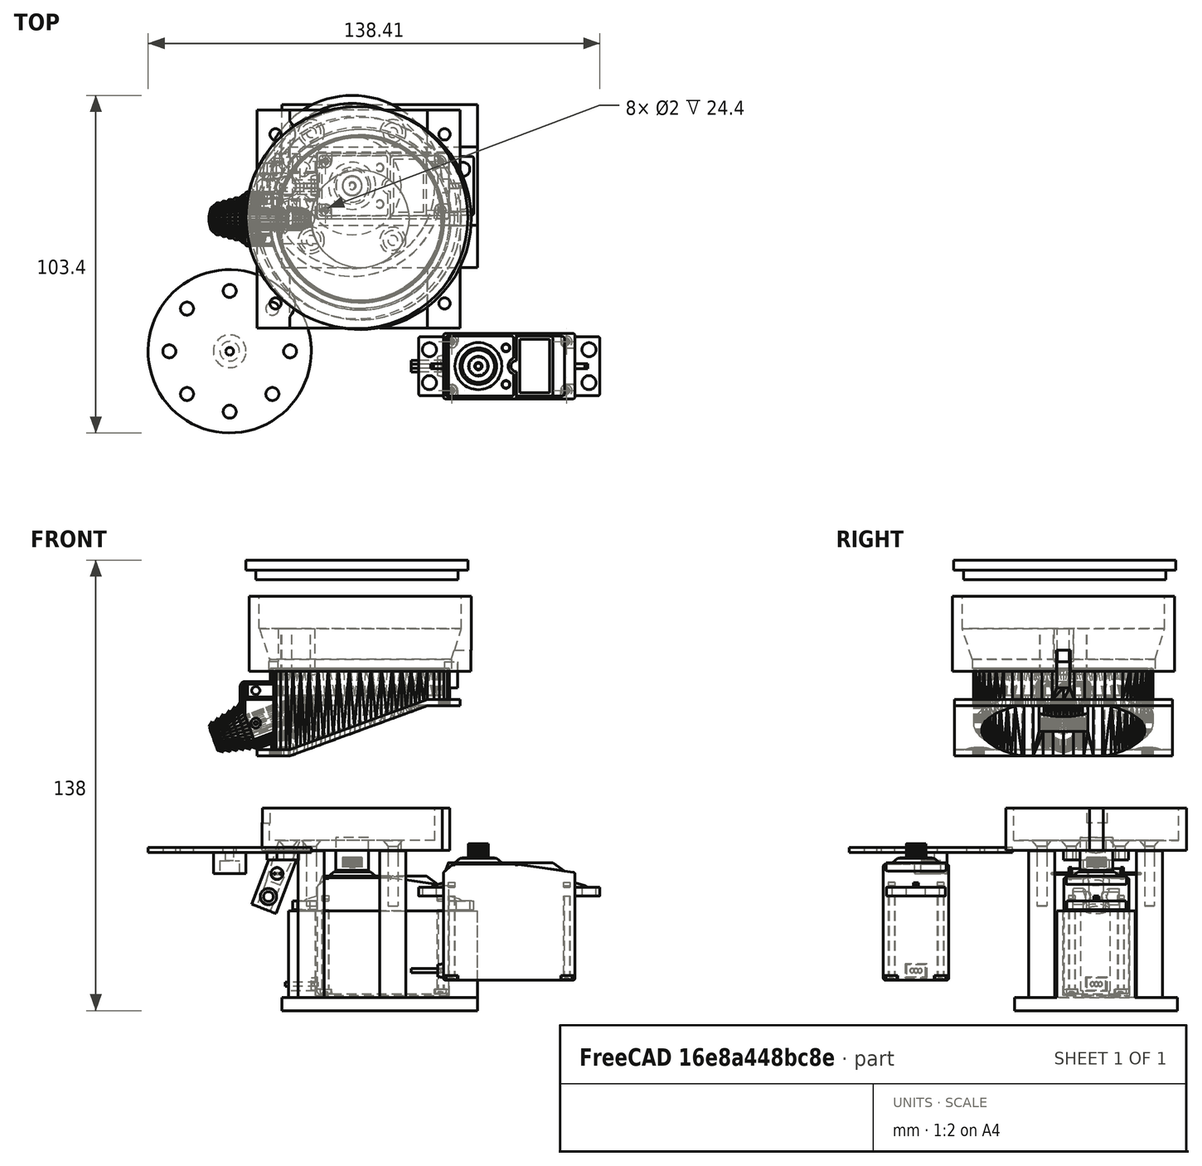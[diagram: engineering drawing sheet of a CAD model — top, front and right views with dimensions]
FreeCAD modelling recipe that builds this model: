
FCSTD DOCUMENT  (FreeCAD 0.21R33694 (Git))
Label: all_parts_chute_with_mount_v4
License: All rights reserved
LicenseURL: http://en.wikipedia.org/wiki/All_rights_reserved
objects: Part::Cylinder×34, Part::Cut×23, Part::MultiFuse×21, Part::Feature×18, Part::Box×11, Part::FeaturePython×5, Part::Cone×2, Sketcher::SketchObject×2, Part::Extrusion×2, Mesh::Feature×1, Part::Fillet×1, Part::Chamfer×1
note: 120 computed .brp shape members not serialized (recipe doc carries the construction recipe); baked Part::Feature solids carry a one-line shape summary decoded from their .brp

FEATURE [Part::Box] Box014  label="Cube014"
  AttacherType = Attacher::AttachEngine3D
  Height = 13
  Length = 4.2
  Placement = pos=(66.2,37.3,63.6) rot=(0,0,1;0rad)
  Width = 4.2
FEATURE [Part::Cylinder] Cylinder022
  Angle = 360
  AttacherType = Attacher::AttachEngine3D
  FirstAngle = 0
  Height = 20
  Placement = pos=(15.5,39.3,51.5) rot=(0,1,0;0.366519rad)
  Radius = 3
  SecondAngle = 0
FEATURE [Part::Box] Box015  label="Cube015"
  AttacherType = Attacher::AttachEngine3D
  Height = 10
  Length = 10
  Placement = pos=(7,36.6,72) rot=(0,0,1;0rad)
  Width = 6.2
FEATURE [Mesh::Feature] Base_V7  label="Base V7"
FEATURE [Part::Feature] Base_V7001_solid  label="hopper (Solid)"
  shape: bbox 76.98 x 66.8 x 28.84 mm, 5900 faces (baked)
FEATURE [Part::Feature] Shape001
  Placement = pos=(47,50.7,-44.8) rot=(0,0,1;3.14159rad)
  shape: bbox 57.75 x 20 x 41.74 mm, 378 faces, 4 solids (baked)
FEATURE [Part::Cylinder] cylinder010  label="servo_central_shaft"
  Angle = 360
  AttacherType = Attacher::AttachEngine3D
  FirstAngle = 0
  Height = 10
  Placement = pos=(37.55,50.7,-7) rot=(0,0,1;0rad)
  Radius = 5
  SecondAngle = 0
FEATURE [Part::Box] Box  label="Cube"
  AttacherType = Attacher::AttachEngine3D
  Height = 27.5
  Length = 58
  Placement = pos=(18,38.6,-47) rot=(0,0,1;0rad)
  Width = 24
FEATURE [Part::Box] Box016  label="Cube016"
  AttacherType = Attacher::AttachEngine3D
  Height = 29.5
  Length = 53
  Placement = pos=(13,46,-44) rot=(0,0,1;0rad)
  Width = 9
FEATURE [Part::Cut] Cut
  Base = -> Box
  Tool = -> Box016
FEATURE [Part::Box] Box017  label="Cube017"
  AttacherType = Attacher::AttachEngine3D
  Height = 29.5
  Length = 10
  Placement = pos=(17,46.6,-46) rot=(0,0,1;0rad)
  Width = 8
FEATURE [Part::Cut] Cut019
  Base = -> Cut
  Tool = -> Box017
FEATURE [Part::Box] Box018  label="Cube018"
  AttacherType = Attacher::AttachEngine3D
  Height = 27.5
  Length = 41
  Placement = pos=(0.5,50.4,-44.2) rot=(0,0,1;0rad)
  Width = 20.4
FEATURE [Part::Fillet] Fillet
  Base = -> Box018
  Edges = 4 edges r=1: [Edge1,Edge3,Edge5,Edge7]
  Placement = pos=(25.85,-9.87885,-1.16822) rot=(0,0,1;0rad)
FEATURE [Part::Cut] Cut020
  Base = -> Cut019
  Tool = -> Fillet
FEATURE [Part::Box] Box020  label="base_plate"
  AttacherType = Attacher::AttachEngine3D
  Height = 4
  Length = 60
  Placement = pos=(16,25.6,-50) rot=(0,0,1;0rad)
  Width = 50
FEATURE [Part::Feature] BOLTS_part  label="Hex socket countersunk head screw M3 20.0"
  Placement = pos=(25,67,2.1) rot=(0,1,0;3.14159rad)
  shape: bbox 6 x 6 x 20 mm, 12 faces (baked)
FEATURE [Part::Feature] BOLTS_part001  label="Hex socket countersunk head screw M3 20.001"
  Placement = pos=(50,67,2.1) rot=(0,1,0;3.14159rad)
  shape: bbox 6 x 6 x 20 mm, 12 faces (baked)
FEATURE [Part::Feature] BOLTS_part002  label="Hex socket countersunk head screw M3 20.002"
  Placement = pos=(50,34,2.1) rot=(0,1,0;3.14159rad)
  shape: bbox 6 x 6 x 20 mm, 12 faces (baked)
FEATURE [Part::Feature] BOLTS_part003  label="Hex socket countersunk head screw M3 20.003"
  Placement = pos=(25,34,2.1) rot=(0,1,0;3.14159rad)
  shape: bbox 6 x 6 x 20 mm, 12 faces (baked)
FEATURE [Part::Cylinder] Cylinder024
  Angle = 360
  AttacherType = Attacher::AttachEngine3D
  FirstAngle = 0
  Height = 48
  Placement = pos=(50,67,-49) rot=(0,0,1;0rad)
  Radius = 4
  SecondAngle = 0
FEATURE [Part::Cylinder] Cylinder025
  Angle = 360
  AttacherType = Attacher::AttachEngine3D
  FirstAngle = 0
  Height = 48
  Placement = pos=(25,34,-49) rot=(0,0,1;0rad)
  Radius = 4
  SecondAngle = 0
FEATURE [Part::Cylinder] Cylinder026
  Angle = 360
  AttacherType = Attacher::AttachEngine3D
  FirstAngle = 0
  Height = 48
  Placement = pos=(25,67,-49) rot=(0,0,1;0rad)
  Radius = 4
  SecondAngle = 0
FEATURE [Part::Cylinder] Cylinder027
  Angle = 360
  AttacherType = Attacher::AttachEngine3D
  FirstAngle = 0
  Height = 48
  Placement = pos=(50,34,-49) rot=(0,0,1;0rad)
  Radius = 4
  SecondAngle = 0
FEATURE [Part::Feature] Shape002  label="led2"
  Placement = pos=(14.5,42.3,-8) rot=(-1,0,0;1.5708rad)
  shape: bbox 3.686 x 11.4 x 3.686 mm, 26 faces, 3 solids (baked)
FEATURE [Part::Feature] Shape003  label="led1"
  Placement = pos=(14.5,59.1,-8) rot=(1,0,0;1.5708rad)
  shape: bbox 3.686 x 11.4 x 3.686 mm, 26 faces, 3 solids (baked)
FEATURE [Part::Feature] BOLTS_part004  label="Hex socket countersunk head screw M3 20.004"
  Placement = pos=(25,34,2.05) rot=(0,1,0;3.14159rad)
  shape: bbox 6 x 6 x 20 mm, 12 faces (baked)
FEATURE [Part::Feature] BOLTS_part005  label="Hex socket countersunk head screw M3 20.005"
  Placement = pos=(50,34,2.05) rot=(0,1,0;3.14159rad)
  shape: bbox 6 x 6 x 20 mm, 12 faces (baked)
FEATURE [Part::Feature] BOLTS_part006  label="Hex socket countersunk head screw M3 20.006"
  Placement = pos=(50,67,2.05) rot=(0,1,0;3.14159rad)
  shape: bbox 6 x 6 x 20 mm, 12 faces (baked)
FEATURE [Part::Feature] BOLTS_part007  label="Hex socket countersunk head screw M3 20.007"
  Placement = pos=(25,67,2.05) rot=(0,1,0;3.14159rad)
  shape: bbox 6 x 6 x 20 mm, 12 faces (baked)
FEATURE [Part::Cylinder] Cylinder032
  Angle = 360
  AttacherType = Attacher::AttachEngine3D
  FirstAngle = 0
  Height = 48
  Placement = pos=(50,67,-43) rot=(0,0,1;0rad)
  Radius = 1.4
  SecondAngle = 0
FEATURE [Part::Cylinder] Cylinder033
  Angle = 360
  AttacherType = Attacher::AttachEngine3D
  FirstAngle = 0
  Height = 48
  Placement = pos=(25,34,-43) rot=(0,0,1;0rad)
  Radius = 1.4
  SecondAngle = 0
FEATURE [Part::Cylinder] Cylinder034
  Angle = 360
  AttacherType = Attacher::AttachEngine3D
  FirstAngle = 0
  Height = 48
  Placement = pos=(25,67,-42) rot=(0,0,1;0rad)
  Radius = 1.4
  SecondAngle = 0
FEATURE [Part::Cylinder] Cylinder035
  Angle = 360
  AttacherType = Attacher::AttachEngine3D
  FirstAngle = 0
  Height = 48
  Placement = pos=(50,34,-43) rot=(0,0,1;0rad)
  Radius = 1.4
  SecondAngle = 0
FEATURE [Part::Cut] Cut030
  Base = -> Cylinder024
  Tool = -> BOLTS_part006
FEATURE [Part::Cut] Cut031
  Base = -> Cylinder025
  Tool = -> BOLTS_part004
FEATURE [Part::Cut] Cut032
  Base = -> Cylinder026
  Tool = -> BOLTS_part007
FEATURE [Part::Cut] Cut033
  Base = -> Cylinder027
  Tool = -> BOLTS_part005
FEATURE [Part::MultiFuse] Fusion011  label="motor_holder"
  Shapes = -> [Cut020,Cut030,Cut031,Cut032,Cut033,Box020]
FEATURE [Part::Cylinder] Cylinder039
  Angle = 360
  AttacherType = Attacher::AttachEngine3D
  FirstAngle = 0
  Height = 21
  Placement = pos=(0,10,4) rot=(1,0,0;1.5708rad)
  Radius = 1.5
  SecondAngle = 0
FEATURE [Part::FeaturePython] Tube003  # WARN: FeaturePython — macro-defined, semantics opaque (R4)
  AttacherType = Attacher::AttachEngine3D
  Height = 5
  InnerRadius = 1.5
  OuterRadius = 2.5
  Placement = pos=(0,2.05,4) rot=(-1,0,0;1.5708rad)
FEATURE [Part::FeaturePython] Tube004  # WARN: FeaturePython — macro-defined, semantics opaque (R4)
  AttacherType = Attacher::AttachEngine3D
  Height = 5
  InnerRadius = 1.5
  OuterRadius = 2.5
  Placement = pos=(0,-2.05,4) rot=(1,0,0;1.5708rad)
FEATURE [Part::Box] Box021  label="Cube019"
  AttacherType = Attacher::AttachEngine3D
  Height = 10
  Length = 20
  Placement = pos=(1.17,-11.94,17.9) rot=(0,0,1;0rad)
  Width = 24
FEATURE [Part::FeaturePython] Tube001  # WARN: FeaturePython — macro-defined, semantics opaque (R4)
  AttacherType = Attacher::AttachEngine3D
  Height = 3
  InnerRadius = 15
  OuterRadius = 27.7
  Placement = pos=(40.45,39.4,63.6) rot=(0,0,1;0rad)
FEATURE [Part::FeaturePython] Tube002  # WARN: FeaturePython — macro-defined, semantics opaque (R4)
  AttacherType = Attacher::AttachEngine3D
  Height = 13
  InnerRadius = 25.3
  OuterRadius = 27.7
  Placement = pos=(40.45,39.4,63.6) rot=(0,0,1;0rad)
FEATURE [Part::MultiFuse] Fusion009
  Shapes = -> [Box014,Tube001,Tube002]
FEATURE [Part::Cut] Cut014  label="cut"
  Base = -> Fusion009
  Tool = -> Cylinder022
FEATURE [Part::Cut] Cut036
  Base = -> Cut014
  Placement = pos=(-2.9,11.3,-64.5) rot=(0,0,1;0rad)
  Tool = -> Box015
FEATURE [Part::MultiFuse] Fusion
  Shapes = -> [BOLTS_part003,Cylinder033]
FEATURE [Part::MultiFuse] Fusion013
  Shapes = -> [BOLTS_part002,Cylinder035]
FEATURE [Part::MultiFuse] Fusion014
  Shapes = -> [BOLTS_part001,Cylinder032]
FEATURE [Part::MultiFuse] Fusion015
  Shapes = -> [BOLTS_part,Cylinder034]
FEATURE [Part::Cut] Cut037
  Base = -> Cut036
  Tool = -> Fusion
FEATURE [Part::Cut] Cut038
  Base = -> Cut037
  Tool = -> Fusion013
FEATURE [Part::Cut] Cut039
  Base = -> Cut038
  Tool = -> Fusion015
FEATURE [Part::Cut] Cut040
  Base = -> Cut039
  Tool = -> Fusion014
FEATURE [Part::Feature] BOLTS_part009  label="Hex socket countersunk head screw M3 20.008"
  Placement = pos=(50,34,2.1) rot=(0,1,0;3.14159rad)
  shape: bbox 6 x 6 x 20 mm, 12 faces (baked)
FEATURE [Part::Cylinder] Cylinder040
  Angle = 360
  AttacherType = Attacher::AttachEngine3D
  FirstAngle = 0
  Height = 48
  Placement = pos=(50,34,-43) rot=(0,0,1;0rad)
  Radius = 1.4
  SecondAngle = 0
FEATURE [Part::MultiFuse] Fusion016
  Placement = pos=(-32,9,0) rot=(0,0,1;0rad)
  Shapes = -> [BOLTS_part009,Cylinder040]
FEATURE [Part::Feature] BOLTS_part010  label="Hex socket countersunk head screw M3 20.009"
  Placement = pos=(50,34,2.1) rot=(0,1,0;3.14159rad)
  shape: bbox 6 x 6 x 20 mm, 12 faces (baked)
FEATURE [Part::Cylinder] Cylinder041
  Angle = 360
  AttacherType = Attacher::AttachEngine3D
  FirstAngle = 0
  Height = 48
  Placement = pos=(50,34,-43) rot=(0,0,1;0rad)
  Radius = 1.4
  SecondAngle = 0
FEATURE [Part::MultiFuse] Fusion017
  Placement = pos=(-32,24,0) rot=(0,0,1;0rad)
  Shapes = -> [BOLTS_part010,Cylinder041]
FEATURE [Part::Box] Box022  label="Cube020"
  AttacherType = Attacher::AttachEngine3D
  Height = 3
  Length = 10
  Placement = pos=(3,-10,15) rot=(0,0,1;0rad)
  Width = 20
FEATURE [Part::Cylinder] Cylinder
  Angle = 360
  AttacherType = Attacher::AttachEngine3D
  FirstAngle = 0
  Height = 18
  Radius = 4
  SecondAngle = 0
FEATURE [Part::Cut] Cut043
  Base = -> Cylinder
  Tool = -> Cylinder039
FEATURE [Part::MultiFuse] Fusion018
  Placement = pos=(2,0,0) rot=(0,1,0;0.366519rad)
  Shapes = -> [Tube003,Tube004,Cut043]
FEATURE [Part::MultiFuse] Fusion019
  Shapes = -> [Fusion018,Box022]
FEATURE [Part::Feature] BOLTS_part011  label="Hex socket countersunk head screw M3 20.010"
  Placement = pos=(50,34,2.1) rot=(0,1,0;3.14159rad)
  shape: bbox 6 x 6 x 20 mm, 12 faces (baked)
FEATURE [Part::Cylinder] Cylinder044
  Angle = 360
  AttacherType = Attacher::AttachEngine3D
  FirstAngle = 0
  Height = 48
  Placement = pos=(50,34,-43) rot=(0,0,1;0rad)
  Radius = 1.4
  SecondAngle = 0
FEATURE [Part::MultiFuse] Fusion021
  Placement = pos=(-32,9,0) rot=(0,0,1;0rad)
  Shapes = -> [BOLTS_part011,Cylinder044]
FEATURE [Part::Feature] BOLTS_part012  label="Hex socket countersunk head screw M3 20.011"
  Placement = pos=(50,34,2.1) rot=(0,1,0;3.14159rad)
  shape: bbox 6 x 6 x 20 mm, 12 faces (baked)
FEATURE [Part::Cylinder] Cylinder045
  Angle = 360
  AttacherType = Attacher::AttachEngine3D
  FirstAngle = 0
  Height = 48
  Placement = pos=(50,34,-43) rot=(0,0,1;0rad)
  Radius = 1.4
  SecondAngle = 0
FEATURE [Part::MultiFuse] Fusion022
  Placement = pos=(-32,24,0) rot=(0,0,1;0rad)
  Shapes = -> [BOLTS_part012,Cylinder045]
FEATURE [Part::Cut] Cut047
  Base = -> Cut040
  Tool = -> Fusion016
FEATURE [Part::Cut] Cut048  label="base"
  Base = -> Cut047
  Tool = -> Fusion017
FEATURE [Part::Feature] Shape004
  Placement = pos=(85.6641,-4.55315,-40.6487) rot=(0,0,1;3.14159rad)
  shape: bbox 57.75 x 20 x 41.74 mm, 378 faces, 4 solids (baked)
FEATURE [Part::Box] Box012  label="Cube012"
  AttacherType = Attacher::AttachEngine3D
  Height = 10
  Length = 10
  Placement = pos=(7,36.17,76) rot=(0,0,1;0rad)
  Width = 6
FEATURE [Part::Box] Box013  label="Cube013"
  AttacherType = Attacher::AttachEngine3D
  Height = 10
  Length = 14
  Placement = pos=(64,38.5,50.5) rot=(0,0,1;0rad)
  Width = 4.3
FEATURE [Part::Cone] Cone
  Angle = 360
  AttacherType = Attacher::AttachEngine3D
  Height = 14
  Placement = pos=(40,40.65,53) rot=(0,0,1;0rad)
  Radius1 = 26.5
  Radius2 = 31
FEATURE [Part::Cylinder] Cylinder019
  Angle = 360
  AttacherType = Attacher::AttachEngine3D
  FirstAngle = 0
  Height = 13
  Placement = pos=(40,40.65,54) rot=(0,0,1;0rad)
  Radius = 34
  SecondAngle = 0
FEATURE [Part::Cylinder] Cylinder020
  Angle = 360
  AttacherType = Attacher::AttachEngine3D
  FirstAngle = 0
  Height = 13
  Placement = pos=(40,39.2,54) rot=(0,0,1;0rad)
  Radius = 25
  SecondAngle = 0
FEATURE [Part::Cylinder] Cylinder021
  Angle = 360
  AttacherType = Attacher::AttachEngine3D
  FirstAngle = 0
  Height = 4
  Placement = pos=(40,40.65,54) rot=(0,0,1;0rad)
  Radius = 28
  SecondAngle = 0
FEATURE [Sketcher::SketchObject] Sketch001
  FullyConstrained = true
  MapMode = 2
  Placement = pos=(0,5,65) rot=(0,0,1;0rad)
  sketch-geometry (8):
    g0: ArcOfCircle CenterX=20.555 CenterY=41.4363 CenterZ=0 NormalX=0 NormalY=0 NormalZ=1 AngleXU=0 Radius=4.5 StartAngle=3.17145 EndAngle=4.38602
    g1: ArcOfCircle CenterX=24.0176 CenterY=34.022 CenterZ=0 NormalX=0 NormalY=0 NormalZ=1 AngleXU=0 Radius=2 StartAngle=5.10518 EndAngle=7.46119
    g2: ArcOfCircle CenterX=20.5312 CenterY=26.882 CenterZ=0 NormalX=0 NormalY=0 NormalZ=1 AngleXU=0 Radius=4.5 StartAngle=1.8916 EndAngle=3.11914
    g3: LineSegment StartX=19.1123 StartY=31.1525 StartZ=0 EndX=24.7831 EndY=32.1743 EndZ=0
    g4: LineSegment StartX=19.1123 StartY=37.1738 StartZ=0 EndX=24.7831 EndY=35.8697 EndZ=0
    g5: LineSegment StartX=16.057 StartY=41.302 StartZ=0 EndX=15.8089 EndY=41.3763 EndZ=0
    g6: LineSegment StartX=15.8133 StartY=26.9187 StartZ=0 EndX=16.0324 EndY=26.9831 EndZ=0
    g7: ArcOfCircle CenterX=39.7432 CenterY=34.1548 CenterZ=0 NormalX=0 NormalY=0 NormalZ=1 AngleXU=0 Radius=25 StartAngle=2.84856 EndAngle=3.43524
  constraints (28):
    c: Coincident(g3,g2)
    c: Coincident(g3,g1)
    c: Coincident(g4,g0)
    c: Coincident(g4,g1)
    c: Coincident(g5,g0)
    c: Coincident(g6,g2)
    c: Coincident(g7,g6)
    c: Coincident(g7,g5)
    c: Radius(g2) = 4.5
    c: Radius(g0) = 4.5
    c: Radius(g1) = 2
    c: Radius(g7) = 25
    c: DistanceX(g5) = 15.8089
    c: DistanceY(g5) = 41.3763
    c: DistanceX(g2) = 16.0324
    c: DistanceY(g2) = 26.9831
    c: DistanceX(g3) = 19.1123
    c: DistanceY(g3) = 31.1525
    c: DistanceX(g2,g0) = 0
    c: DistanceX(g3,g1) = 0
    c: DistanceX(g1) = 24.7831
    c: DistanceY(g1) = 32.1743
    c: DistanceX(g5) = 16.057
    c: DistanceY(g5) = 41.302
    c: DistanceX(g7) = 15.8133
    c: DistanceY(g7) = 26.9187
    c: DistanceY(g1) = 35.8697
    c: DistanceY(g0) = 37.1738
FEATURE [Part::Extrusion] Extrude001
  Base = -> Sketch001
  Dir = (0,0,1)
  DirMode = 2
  FaceMakerClass = Part::FaceMakerBullseye
  LengthFwd = 14
  LengthRev = 0
  Placement = pos=(0,0,7) rot=(0,0,1;0rad)
  Solid = true
  Symmetric = false
FEATURE [Part::MultiFuse] Fusion006  label="pellet_sorter"
  Placement = pos=(0,1.5,-19) rot=(0,0,1;0rad)
  Shapes = -> [Box012,Extrude001]
FEATURE [Part::FeaturePython] Tube  # WARN: FeaturePython — macro-defined, semantics opaque (R4)
  AttacherType = Attacher::AttachEngine3D
  Height = 23
  InnerRadius = 31
  OuterRadius = 34
  Placement = pos=(40,40.65,54) rot=(0,0,1;0rad)
FEATURE [Part::MultiFuse] Fusion010
  Shapes = -> [Tube,Cylinder019,Cylinder020]
FEATURE [Part::Cut] Cut015
  Base = -> Fusion010
  Tool = -> Cone
FEATURE [Part::Cut] Cut016
  Base = -> Cut015
  Tool = -> Cylinder021
FEATURE [Part::MultiFuse] Fusion024
  Shapes = -> [Fusion006,Cut016]
FEATURE [Part::Cut] Cut017  label="lid"
  Base = -> Fusion024
  Tool = -> Box013
FEATURE [Part::Cylinder] Cylinder047
  Angle = 360
  AttacherType = Attacher::AttachEngine3D
  FirstAngle = 0
  Height = 3
  Radius = 34
  SecondAngle = 0
FEATURE [Part::Cylinder] Cylinder048
  Angle = 360
  AttacherType = Attacher::AttachEngine3D
  FirstAngle = 0
  Height = 6
  Radius = 31
  SecondAngle = 0
FEATURE [Part::MultiFuse] Fusion025  label="cap"
  Placement = pos=(39,41,88) rot=(1,0,0;3.14159rad)
  Shapes = -> [Cylinder047,Cylinder048]
FEATURE [Part::Cylinder] cylinder012
  Angle = 360
  AttacherType = Attacher::AttachEngine3D
  FirstAngle = 0
  Height = 1.5
  Radius = 25
  SecondAngle = 0
FEATURE [Part::Cylinder] cylinder013
  Angle = 360
  AttacherType = Attacher::AttachEngine3D
  FirstAngle = 0
  Height = 5
  Placement = pos=(18.5,0,0) rot=(0,0,1;0rad)
  Radius = 2
  SecondAngle = 0
FEATURE [Part::Cylinder] cylinder014
  Angle = 360
  AttacherType = Attacher::AttachEngine3D
  FirstAngle = 0
  Height = 5
  Placement = pos=(13.0815,13.0815,0) rot=(0,0,1;0.785398rad)
  Radius = 2
  SecondAngle = 0
FEATURE [Part::Cylinder] cylinder015
  Angle = 360
  AttacherType = Attacher::AttachEngine3D
  FirstAngle = 0
  Height = 5
  Placement = pos=(0,18.5,0) rot=(0,0,1;1.5708rad)
  Radius = 2
  SecondAngle = 0
FEATURE [Part::Cylinder] cylinder016
  Angle = 360
  AttacherType = Attacher::AttachEngine3D
  FirstAngle = 0
  Height = 5
  Placement = pos=(-13.0815,13.0815,0) rot=(0,0,1;2.35619rad)
  Radius = 2
  SecondAngle = 0
FEATURE [Part::Cylinder] cylinder017
  Angle = 360
  AttacherType = Attacher::AttachEngine3D
  FirstAngle = 0
  Height = 5
  Placement = pos=(-18.5,2e-15,0) rot=(0,0,1;3.14159rad)
  Radius = 2
  SecondAngle = 0
FEATURE [Part::Cylinder] cylinder018
  Angle = 360
  AttacherType = Attacher::AttachEngine3D
  FirstAngle = 0
  Height = 5
  Placement = pos=(-13.0815,-13.0815,0) rot=(0,0,1;3.92699rad)
  Radius = 2
  SecondAngle = 0
FEATURE [Part::Cylinder] cylinder019
  Angle = 360
  AttacherType = Attacher::AttachEngine3D
  FirstAngle = 0
  Height = 5
  Placement = pos=(0,-18.5,0) rot=(0,0,-1;1.5708rad)
  Radius = 2
  SecondAngle = 0
FEATURE [Part::Cylinder] cylinder020
  Angle = 360
  AttacherType = Attacher::AttachEngine3D
  FirstAngle = 0
  Height = 5
  Placement = pos=(13.0815,-13.0815,0) rot=(0,0,-1;0.785398rad)
  Radius = 2
  SecondAngle = 0
FEATURE [Part::MultiFuse] Group001
  Placement = pos=(0,0,-1) rot=(0,0,1;0rad)
  Shapes = -> [cylinder013,cylinder014,cylinder015,cylinder016,cylinder017,cylinder018,cylinder019,cylinder020]
FEATURE [Part::Feature] Shape005
  Placement = pos=(85.6641,-4.55315,-40.6487) rot=(0,0,1;3.14159rad)
  shape: bbox 57.75 x 20 x 41.74 mm, 378 faces, 4 solids (baked)
FEATURE [Part::Cylinder] cylinder021  label="servo_central_shaft002"
  Angle = 360
  AttacherType = Attacher::AttachEngine3D
  FirstAngle = 0
  Height = 8
  Radius = 5
  SecondAngle = 0
FEATURE [Sketcher::SketchObject] Sketch002
  FullyConstrained = false
  MapMode = 5
  Placement = pos=(85.6641,-4.55315,1.09128) rot=(0,0,1;3.14159rad)
  Support = -> [Shape005]
  sketch-geometry (1):
    g0: Circle CenterX=9.4502 CenterY=-0.000218 CenterZ=0 NormalX=0 NormalY=0 NormalZ=1 AngleXU=0 Radius=3
  constraints (1):
    c: Radius(g0) = 3
FEATURE [Part::Extrusion] Extrude002
  Base = -> Sketch002
  Dir = (0,0,1)
  DirMode = 2
  FaceMakerClass = Part::FaceMakerBullseye
  LengthFwd = 6
  LengthRev = 0
  Placement = pos=(-76.21,4.55,3) rot=(0,0,1;0rad)
  Solid = true
  Symmetric = false
FEATURE [Part::Cylinder] Cylinder049
  Angle = 360
  AttacherType = Attacher::AttachEngine3D
  FirstAngle = 0
  Height = 19
  Placement = pos=(0,0,-1) rot=(0,0,1;0rad)
  Radius = 1.2
  SecondAngle = 0
FEATURE [Part::MultiFuse] Fusion026
  Shapes = -> [Group001,Extrude002,Cylinder049]
FEATURE [Part::MultiFuse] Fusion027
  Shapes = -> [cylinder012,cylinder021]
FEATURE [Part::Cut] Cut050  label="rotor001"
  Base = -> Fusion027
  Placement = pos=(0,0,0) rot=(1,0,0;3.14159rad)
  Tool = -> Fusion026
FEATURE [Part::Cone] Cone001
  Angle = 360
  AttacherType = Attacher::AttachEngine3D
  Height = 11
  Placement = pos=(0,-29,0) rot=(0,0,1;0rad)
  Radius1 = 2.25
  Radius2 = 3
FEATURE [Part::Cylinder] Cylinder050
  Angle = 360
  AttacherType = Attacher::AttachEngine3D
  FirstAngle = 0
  Height = 10
  Placement = pos=(0,-29,-10) rot=(0,0,1;0rad)
  Radius = 2.25
  SecondAngle = 0
FEATURE [Part::Cylinder] Cylinder051
  Angle = 360
  AttacherType = Attacher::AttachEngine3D
  FirstAngle = 0
  Height = 14
  Placement = pos=(0,-29,11) rot=(0,0,1;0rad)
  Radius = 3
  SecondAngle = 0
FEATURE [Part::MultiFuse] Fusion028
  Placement = pos=(5,29,8) rot=(0,1,0;0.366519rad)
  Shapes = -> [Cone001,Cylinder050,Cylinder051]
FEATURE [Part::MultiFuse] Fusion020
  Shapes = -> [Box021,Fusion028]
FEATURE [Part::Cut] Cut044  label="foodchute"
  Base = -> Fusion019
  Placement = pos=(8.45427,50.6,-18.8) rot=(0,0,1;0rad)
  Tool = -> Fusion020
FEATURE [Part::Chamfer] Chamfer
  Base = -> Cut044
  Edges = 2 edges r=3: [Edge1,Edge3]
FEATURE [Part::Cut] Cut045
  Base = -> Chamfer
  Tool = -> Fusion021
FEATURE [Part::Cut] Cut046  label="chute_with_mount"
  Base = -> Cut045
  Tool = -> Fusion022
